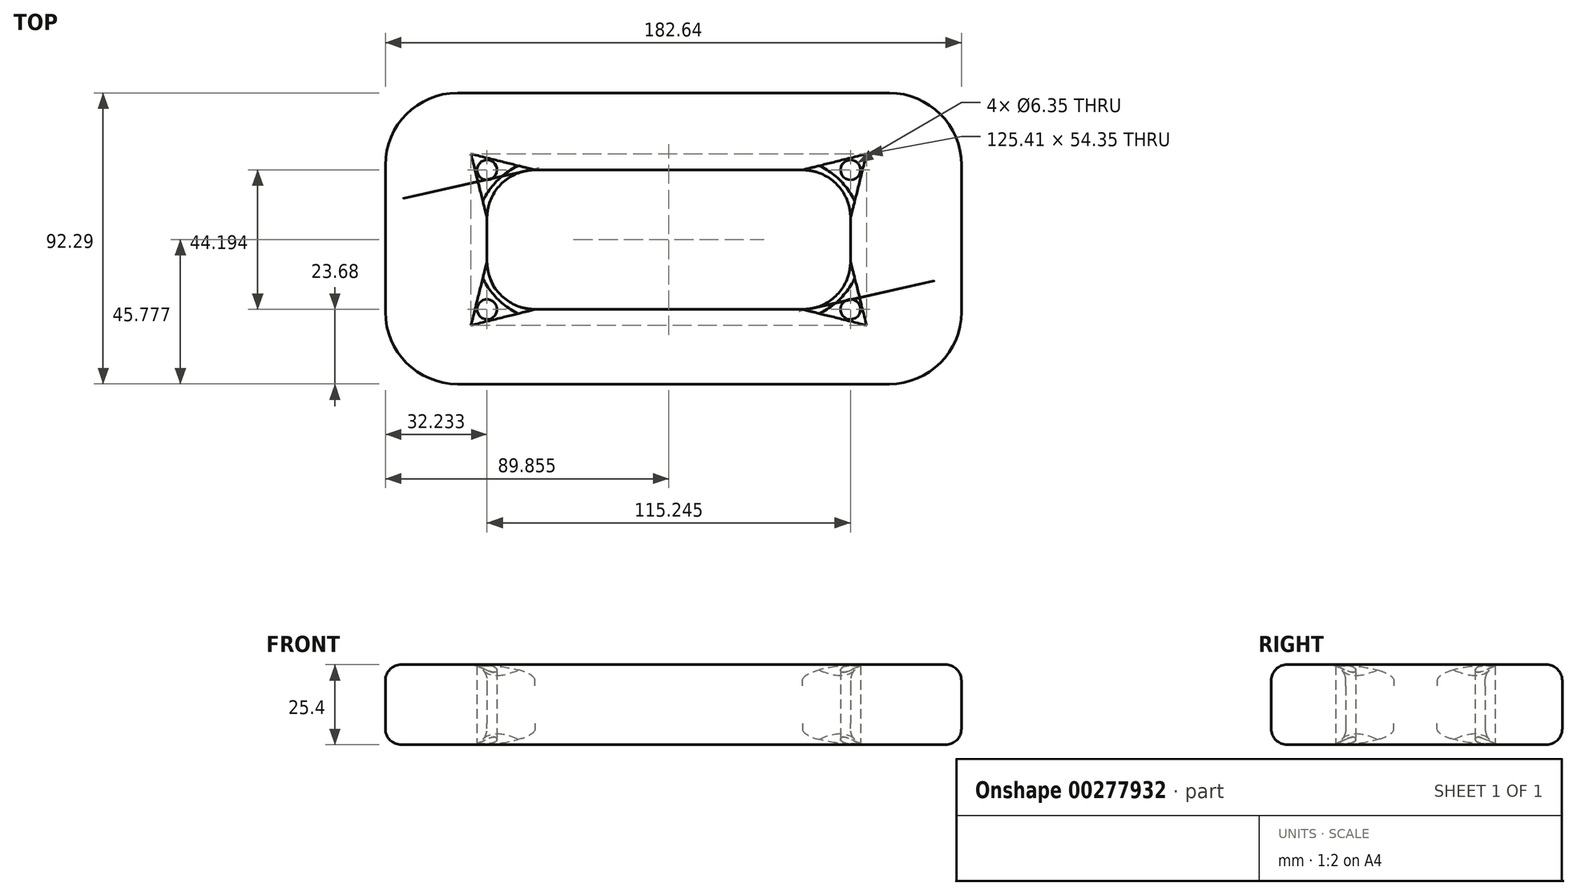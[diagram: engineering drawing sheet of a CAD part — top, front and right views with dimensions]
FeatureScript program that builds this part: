
annotation { "Feature Type Name" : "Feature", "Feature Type Description" : "" }
export const myFeature = defineFeature(function(context is Context, id is Id, definition is map)
    precondition{}
    {
        {
            var Q0;
            Q0=qCreatedBy(makeId("Top.planeOp"),FACE);
            var sketch = newSketch(context, id + "F0", { "sketchPlane" : qUnion([Q0])});
            skLineSegment(sketch, "E0.bottom", {"start": v(-55.55, 26.61) * mm, "end": v(59.7, 26.61) * mm});
            skLineSegment(sketch, "E0.top", {"start": v(-55.55, -17.58) * mm, "end": v(59.7, -17.58) * mm});
            skLineSegment(sketch, "E0.left", {"start": v(-55.55, 26.61) * mm, "end": v(-55.55, -17.58) * mm});
            skLineSegment(sketch, "E0.right", {"start": v(59.7, 26.61) * mm, "end": v(59.7, -17.58) * mm});
            skLineSegment(sketch, "E1.bottom", {"start": v(-87.78, 51.03) * mm, "end": v(94.86, 51.03) * mm});
            skLineSegment(sketch, "E1.top", {"start": v(-87.78, -41.26) * mm, "end": v(94.86, -41.26) * mm});
            skLineSegment(sketch, "E1.left", {"start": v(-87.78, 51.03) * mm, "end": v(-87.78, -41.26) * mm});
            skLineSegment(sketch, "E1.right", {"start": v(94.86, 51.03) * mm, "end": v(94.86, -41.26) * mm});
            skSolve(sketch);
        }
        {
            var Q0;
            Q0=makeQuery(id+"F0.imprint","IMPRINT",FACE,{"disambiguationData":[TD([[makeQuery(id+"F0.imprint","IMPRINT",EDGE,{"derivedFrom":sQuery(id+"F0.wireOp",EDGE,"E0.bottom")}),1.0]])]});
            extrude(context, id + "F1", {"entities" : qUnion([Q0]), "depth" : 25.4 * mm});
        }
        {
            var Q0;
            Q0=makeQuery(id+"F1.opExtrude","CAP_EDGE",EDGE,{"disambiguationData":[OSD([sQuery(id+"F0.wireOp",EDGE,"E0.bottom")])],"isStart":false});
            var Q1;
            Q1=makeQuery(id+"F1.opExtrude","CAP_EDGE",EDGE,{"disambiguationData":[OSD([sQuery(id+"F0.wireOp",EDGE,"E0.left")])],"isStart":false});
            var Q2;
            Q2=makeQuery(id+"F1.opExtrude","CAP_EDGE",EDGE,{"disambiguationData":[OSD([sQuery(id+"F0.wireOp",EDGE,"E0.right")])],"isStart":false});
            var Q3;
            Q3=makeQuery(id+"F1.opExtrude","CAP_EDGE",EDGE,{"disambiguationData":[OSD([sQuery(id+"F0.wireOp",EDGE,"E0.top")])],"isStart":false});
            var Q4;
            Q4=makeQuery(id+"F1.opExtrude","CAP_EDGE",EDGE,{"disambiguationData":[OSD([sQuery(id+"F0.wireOp",EDGE,"E1.bottom")])],"isStart":false});
            var Q5;
            Q5=makeQuery(id+"F1.opExtrude","CAP_EDGE",EDGE,{"disambiguationData":[OSD([sQuery(id+"F0.wireOp",EDGE,"E1.right")])],"isStart":false});
            var Q6;
            Q6=makeQuery(id+"F1.opExtrude","CAP_EDGE",EDGE,{"disambiguationData":[OSD([sQuery(id+"F0.wireOp",EDGE,"E1.top")])],"isStart":false});
            var Q7;
            Q7=makeQuery(id+"F1.opExtrude","CAP_EDGE",EDGE,{"disambiguationData":[OSD([sQuery(id+"F0.wireOp",EDGE,"E1.left")])],"isStart":false});
            var Q8;
            Q8=makeQuery(id+"F1.opExtrude","CAP_EDGE",EDGE,{"disambiguationData":[OSD([sQuery(id+"F0.wireOp",EDGE,"E1.top")])],"isStart":true});
            var Q9;
            Q9=makeQuery(id+"F1.opExtrude","CAP_FACE",FACE,{"disambiguationData":[OSD([sQuery(id+"F0.wireOp",EDGE,"E0.bottom"),sQuery(id+"F0.wireOp",EDGE,"E0.top"),sQuery(id+"F0.wireOp",EDGE,"E0.left"),sQuery(id+"F0.wireOp",EDGE,"E0.right"),sQuery(id+"F0.wireOp",EDGE,"E1.bottom"),sQuery(id+"F0.wireOp",EDGE,"E1.top"),sQuery(id+"F0.wireOp",EDGE,"E1.left"),sQuery(id+"F0.wireOp",EDGE,"E1.right")])],"isStart":true});
            fillet(context, id + "F2", {"entities" : qUnion([Q0, Q1, Q2, Q3, Q4, Q5, Q6, Q7, Q8, Q9]), "radius" : 5.08 * mm, "tangentPropagation" : true, "allowEdgeOverflow" : false});
        }
        {
            var Q0;
            Q0=makeQuery(id+"F1.opExtrude","SWEPT_EDGE",EDGE,{"disambiguationData":[OSD([sQuery(id+"F0.wireOp",EDGE,"E1.top"),sQuery(id+"F0.wireOp",EDGE,"E1.left")])]});
            var Q1;
            Q1=makeQuery(id+"F1.opExtrude","SWEPT_EDGE",EDGE,{"disambiguationData":[OSD([sQuery(id+"F0.wireOp",EDGE,"E1.bottom"),sQuery(id+"F0.wireOp",EDGE,"E1.right")])]});
            var Q2;
            Q2=makeQuery(id+"F1.opExtrude","SWEPT_EDGE",EDGE,{"disambiguationData":[OSD([sQuery(id+"F0.wireOp",EDGE,"E1.top"),sQuery(id+"F0.wireOp",EDGE,"E1.right")])]});
            var Q3;
            Q3=makeQuery(id+"F1.opExtrude","SWEPT_EDGE",EDGE,{"disambiguationData":[OSD([sQuery(id+"F0.wireOp",EDGE,"E1.bottom"),sQuery(id+"F0.wireOp",EDGE,"E1.left")])]});
            var Q4;
            {var subQ0=sQuery(id+"F0.wireOp",EDGE,"E1.top");Q4=makeQuery(id+"F2.opFillet","BLEND_EDGE",EDGE,{"blendedFrom":[makeQuery(id+"F1.opExtrude","CAP_EDGE",EDGE,{"disambiguationData":[OSD([subQ0])],"isStart":false}),makeQuery(id+"F1.opExtrude","CAP_FACE",FACE,{"disambiguationData":[OSD([sQuery(id+"F0.wireOp",EDGE,"E0.bottom"),sQuery(id+"F0.wireOp",EDGE,"E0.top"),sQuery(id+"F0.wireOp",EDGE,"E0.left"),sQuery(id+"F0.wireOp",EDGE,"E0.right"),sQuery(id+"F0.wireOp",EDGE,"E1.bottom"),subQ0,sQuery(id+"F0.wireOp",EDGE,"E1.left"),sQuery(id+"F0.wireOp",EDGE,"E1.right")])],"isStart":false})],"blendedInto":[makeQuery(id+"F1.opExtrude","CAP_FACE",FACE,{"disambiguationData":[OSD([sQuery(id+"F0.wireOp",EDGE,"E0.bottom"),sQuery(id+"F0.wireOp",EDGE,"E0.top"),sQuery(id+"F0.wireOp",EDGE,"E0.left"),sQuery(id+"F0.wireOp",EDGE,"E0.right"),sQuery(id+"F0.wireOp",EDGE,"E1.bottom"),subQ0,sQuery(id+"F0.wireOp",EDGE,"E1.left"),sQuery(id+"F0.wireOp",EDGE,"E1.right")])],"isStart":false})]});}
            var Q5;
            {var subQ0=sQuery(id+"F0.wireOp",EDGE,"E1.top");Q5=makeQuery(id+"F2.opFillet","BLEND_EDGE",EDGE,{"blendedFrom":[makeQuery(id+"F1.opExtrude","CAP_EDGE",EDGE,{"disambiguationData":[OSD([subQ0])],"isStart":false}),makeQuery(id+"F1.opExtrude","SWEPT_FACE",FACE,{"disambiguationData":[OSD([subQ0])]})],"blendedInto":[makeQuery(id+"F1.opExtrude","SWEPT_FACE",FACE,{"disambiguationData":[OSD([subQ0])]})]});}
            fillet(context, id + "F3", {"entities" : qUnion([Q0, Q1, Q2, Q3, Q4, Q5]), "radius" : 22.86 * mm, "tangentPropagation" : true, "allowEdgeOverflow" : false});
        }
        {
            var Q0;
            Q0=makeQuery(id+"F1.opExtrude","SWEPT_EDGE",EDGE,{"disambiguationData":[OSD([sQuery(id+"F0.wireOp",EDGE,"E0.top"),sQuery(id+"F0.wireOp",EDGE,"E0.right")])]});
            var Q1;
            Q1=makeQuery(id+"F1.opExtrude","SWEPT_EDGE",EDGE,{"disambiguationData":[OSD([sQuery(id+"F0.wireOp",EDGE,"E0.top"),sQuery(id+"F0.wireOp",EDGE,"E0.left")])]});
            var Q2;
            Q2=makeQuery(id+"F1.opExtrude","SWEPT_EDGE",EDGE,{"disambiguationData":[OSD([sQuery(id+"F0.wireOp",EDGE,"E0.bottom"),sQuery(id+"F0.wireOp",EDGE,"E0.right")])]});
            var Q3;
            Q3=makeQuery(id+"F1.opExtrude","SWEPT_EDGE",EDGE,{"disambiguationData":[OSD([sQuery(id+"F0.wireOp",EDGE,"E0.bottom"),sQuery(id+"F0.wireOp",EDGE,"E0.left")])]});
            fillet(context, id + "F4", {"entities" : qUnion([Q0, Q1, Q2, Q3]), "radius" : 15.24 * mm, "tangentPropagation" : true, "allowEdgeOverflow" : false});
        }
        {
            var Q0;
            Q0=sQuery(id+"F0.wireOp",VERTEX,"E0.right.end");
            var Q1;
            Q1=sQuery(id+"F0.wireOp",VERTEX,"E0.right.start");
            var Q2;
            Q2=sQuery(id+"F0.wireOp",VERTEX,"E0.left.start");
            var Q3;
            Q3=sQuery(id+"F0.wireOp",VERTEX,"E0.left.end");
            var Q4;
            Q4=makeQuery(id+"F1.opExtrude","SWEPT_BODY",BODY,{"disambiguationData":[OSD([sQuery(id+"F0.wireOp",EDGE,"E0.bottom"),sQuery(id+"F0.wireOp",EDGE,"E0.top"),sQuery(id+"F0.wireOp",EDGE,"E0.left"),sQuery(id+"F0.wireOp",EDGE,"E0.right"),sQuery(id+"F0.wireOp",EDGE,"E1.bottom"),sQuery(id+"F0.wireOp",EDGE,"E1.top"),sQuery(id+"F0.wireOp",EDGE,"E1.left"),sQuery(id+"F0.wireOp",EDGE,"E1.right")])]});
            hole(context, id + "F5", {"style" : HoleStyle.SIMPLE, "endStyle" : HoleEndStyle.THROUGH, "oppositeDirection" : true, "holeDiameter" : 6.35 * mm, "tappedDepth" : 12.7 * mm, "tapClearance" : 3, "locations" : qUnion([Q0, Q1, Q2, Q3]), "scope" : qUnion([Q4])});
        }
    });
